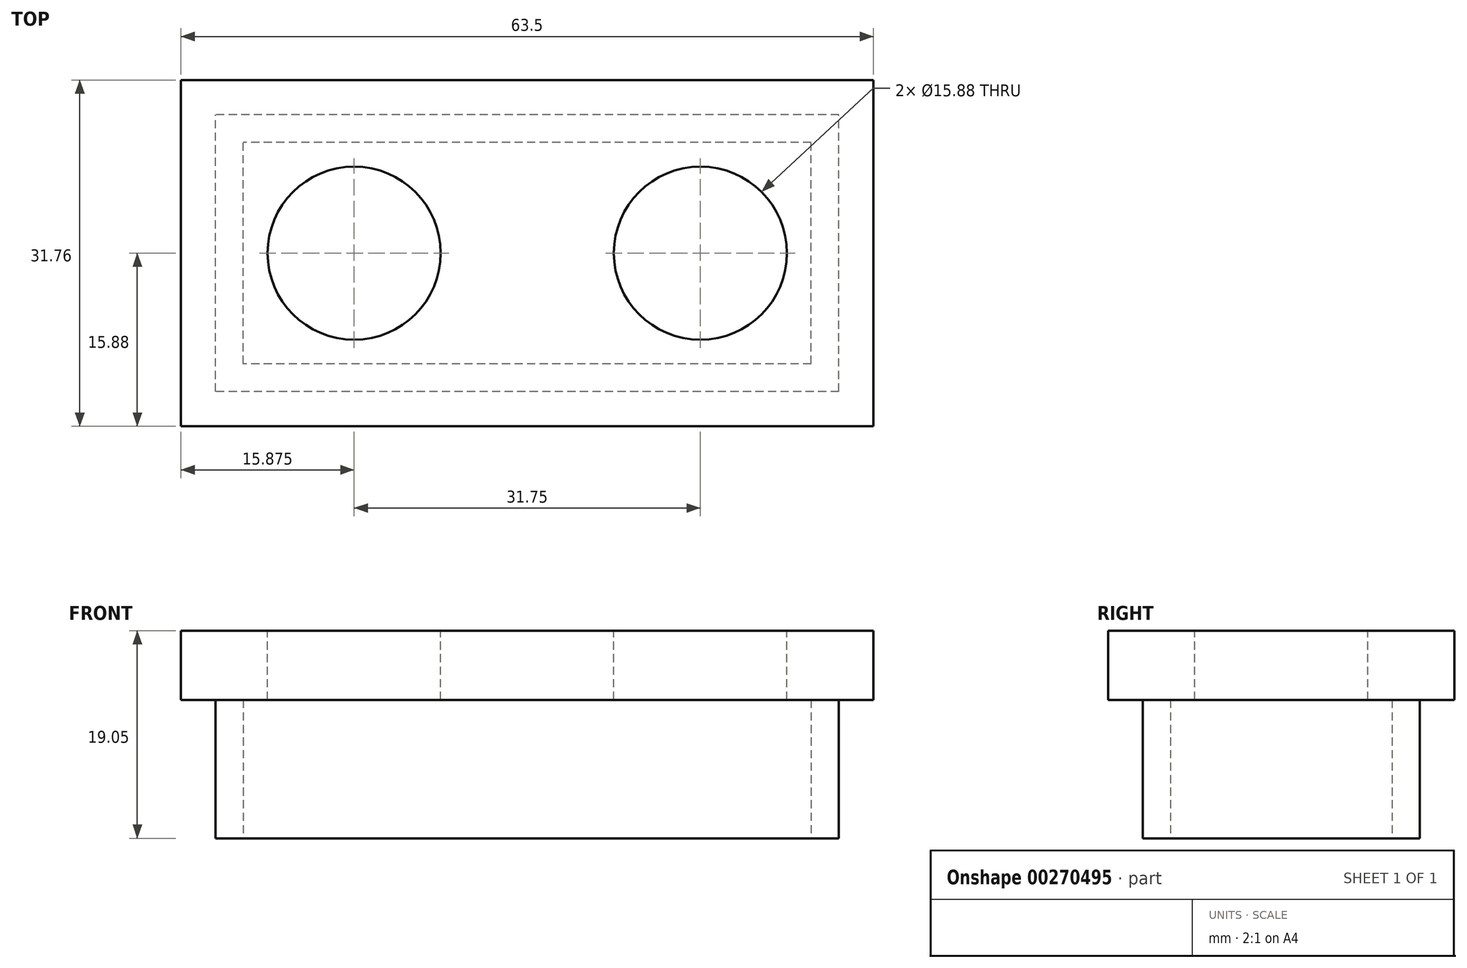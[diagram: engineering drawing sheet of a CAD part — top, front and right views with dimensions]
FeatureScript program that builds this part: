
annotation { "Feature Type Name" : "Feature", "Feature Type Description" : "" }
export const myFeature = defineFeature(function(context is Context, id is Id, definition is map)
    precondition{}
    {
        {
            var Q0;
            Q0=qCreatedBy(makeId("Top.planeOp"),FACE);
            var sketch = newSketch(context, id + "F0", { "sketchPlane" : qUnion([Q0])});
            skLineSegment(sketch, "E0.bottom", {"start": v(28.58, -12.7) * mm, "end": v(-28.58, -12.7) * mm});
            skLineSegment(sketch, "E0.top", {"start": v(28.57, 12.7) * mm, "end": v(-28.58, 12.7) * mm});
            skLineSegment(sketch, "E0.left", {"start": v(28.58, -12.7) * mm, "end": v(28.57, 12.7) * mm});
            skLineSegment(sketch, "E0.right", {"start": v(-28.57, -12.7) * mm, "end": v(-28.58, 12.7) * mm});
            skPoint(sketch, "E0.middle", {"position": v(0, 0) * mm});
            skSolve(sketch);
        }
        {
            var Q0;
            Q0=makeQuery(id+"F0.imprint","IMPRINT",FACE,{"disambiguationData":[TD([[makeQuery(id+"F0.imprint","IMPRINT",EDGE,{"derivedFrom":sQuery(id+"F0.wireOp",EDGE,"E0.bottom")}),-1.0]])]});
            extrude(context, id + "F1", {"entities" : qUnion([Q0]), "depth" : 12.7 * mm});
        }
        {
            var Q0;
            Q0=makeQuery(id+"F1.opExtrude","CAP_FACE",FACE,{"disambiguationData":[OSD([sQuery(id+"F0.wireOp",EDGE,"E0.bottom"),sQuery(id+"F0.wireOp",EDGE,"E0.top"),sQuery(id+"F0.wireOp",EDGE,"E0.left"),sQuery(id+"F0.wireOp",EDGE,"E0.right")])],"isStart":false});
            var sketch = newSketch(context, id + "F2", { "sketchPlane" : qUnion([Q0])});
            skLineSegment(sketch, "E1.bottom", {"start": v(31.75, -15.88) * mm, "end": v(-31.75, -15.88) * mm});
            skLineSegment(sketch, "E1.top", {"start": v(31.75, 15.88) * mm, "end": v(-31.75, 15.88) * mm});
            skLineSegment(sketch, "E1.left", {"start": v(31.75, -15.88) * mm, "end": v(31.75, 15.88) * mm});
            skLineSegment(sketch, "E1.right", {"start": v(-31.75, -15.88) * mm, "end": v(-31.75, 15.88) * mm});
            skPoint(sketch, "E1.middle", {"position": v(0, 0) * mm});
            skSolve(sketch);
        }
        {
            var Q0;
            Q0=makeQuery(id+"F2.imprint","IMPRINT",FACE,{"disambiguationData":[TD([[makeQuery(id+"F2.imprint","IMPRINT",EDGE,{"derivedFrom":sQuery(id+"F2.wireOp",EDGE,"E1.bottom")}),-1.0]])]});
            var Q1;
            Q1=makeQuery(id+"F2.imprint","IMPRINT",FACE,{"disambiguationData":[TD([[makeQuery(id+"F2.imprint","IMPRINT",EDGE,{"derivedFrom":makeQuery(id+"F1.opExtrude","CAP_EDGE",EDGE,{"disambiguationData":[OSD([sQuery(id+"F0.wireOp",EDGE,"E0.bottom")])],"isStart":false})}),-1.0]])]});
            extrude(context, id + "F3", {"entities" : qUnion([Q0, Q1]), "operationType" : NewBodyOperationType.ADD, "depth" : 6.35 * mm});
        }
        {
            var Q0;
            Q0=makeQuery(id+"F3.opExtrude","CAP_FACE",FACE,{"disambiguationData":[OSD([sQuery(id+"F2.wireOp",EDGE,"E1.bottom"),sQuery(id+"F2.wireOp",EDGE,"E1.top"),sQuery(id+"F2.wireOp",EDGE,"E1.left"),sQuery(id+"F2.wireOp",EDGE,"E1.right")])],"isStart":false});
            var sketch = newSketch(context, id + "F4", { "sketchPlane" : qUnion([Q0])});
            skCircle(sketch, "E2", {"center": v(-15.88, 0) * mm, "radius": 7.94 * mm});
            skCircle(sketch, "E3", {"center": v(15.88, 0) * mm, "radius": 7.94 * mm});
            skLineSegment(sketch, "E4", {"start": v(0, 0) * mm, "end": v(0, 24.65) * mm, "construction": true});
            skSolve(sketch);
        }
        {
            var Q0;
            Q0=makeQuery(id+"F4.imprint","IMPRINT",FACE,{"disambiguationData":[TD([[makeQuery(id+"F4.imprint","IMPRINT",EDGE,{"derivedFrom":sQuery(id+"F4.wireOp",EDGE,"E2")}),1.0]])]});
            var Q1;
            Q1=makeQuery(id+"F4.imprint","IMPRINT",FACE,{"disambiguationData":[TD([[makeQuery(id+"F4.imprint","IMPRINT",EDGE,{"derivedFrom":sQuery(id+"F4.wireOp",EDGE,"E3")}),1.0]])]});
            extrude(context, id + "F5", {"entities" : qUnion([Q0, Q1]), "operationType" : NewBodyOperationType.REMOVE, "endBound" : BoundingType.THROUGH_ALL, "oppositeDirection" : true, "depth" : 25.4 * mm});
        }
        {
            var Q0;
            Q0=makeQuery(id+"F1.opExtrude","CAP_FACE",FACE,{"disambiguationData":[OSD([sQuery(id+"F0.wireOp",EDGE,"E0.bottom"),sQuery(id+"F0.wireOp",EDGE,"E0.top"),sQuery(id+"F0.wireOp",EDGE,"E0.left"),sQuery(id+"F0.wireOp",EDGE,"E0.right")])],"isStart":true});
            var sketch = newSketch(context, id + "F6", { "sketchPlane" : qUnion([Q0])});
            skCircle(sketch, "E5.0", {"center": v(15.88, 0) * mm, "radius": 7.94 * mm});
            skCircle(sketch, "E5.1", {"center": v(-15.88, 0) * mm, "radius": 7.94 * mm});
            skLineSegment(sketch, "E6.0", {"start": v(26.04, -10.16) * mm, "end": v(-26.04, -10.16) * mm});
            skLineSegment(sketch, "E6.1", {"start": v(26.04, 10.16) * mm, "end": v(26.04, -10.16) * mm});
            skLineSegment(sketch, "E6.2", {"start": v(26.04, 10.16) * mm, "end": v(-26.04, 10.16) * mm});
            skLineSegment(sketch, "E6.3", {"start": v(-26.04, 10.16) * mm, "end": v(-26.04, -10.16) * mm});
            skSolve(sketch);
        }
        {
            var Q0;
            Q0=makeQuery(id+"F6.imprint","IMPRINT",FACE,{"disambiguationData":[TD([[makeQuery(id+"F6.imprint","IMPRINT",EDGE,{"derivedFrom":sQuery(id+"F6.wireOp",EDGE,"E5.0")}),1.0]])]});
            extrude(context, id + "F7", {"entities" : qUnion([Q0]), "operationType" : NewBodyOperationType.REMOVE, "oppositeDirection" : true, "depth" : 12.7 * mm});
        }
    });
